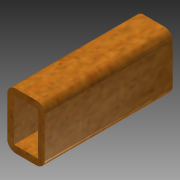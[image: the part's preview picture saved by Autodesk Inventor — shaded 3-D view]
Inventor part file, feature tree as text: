
AUTODESK INVENTOR PART (.ipt)
format: ipt  version: 2015 (Build 190159000, 159)  size: 113,152 bytes
history: native  units: in
note: dims shown in document units (in); Inventor stores cm internally (conversion verified against a paired STEP export)
features: reference x4, sketch x1, plane x1, extrude x1, fillet x1
ambient origin geometry x8: Origin, YZ Plane, XZ Plane, XY Plane, X Axis, Y Axis, Z Axis, Center Point
bodies: Solid1 (feature_tree)
feature tree (8):
  sketch  "Sketch1"  dims[d0=0.1in d1=0.0in d2=0.0in d3=0.125in]
  plane  "Work Plane1"
  extrude  "Extrusion1"  TaperAngle=0.0deg  [1 undecoded]
  fillet  "Fillet1"  Radius=0.125in
  reference  "Reference1"
  reference  "Reference2"
  reference  "Reference3"
  reference  "Reference4"
note: 1 required parameter value undecoded (feature->parameter linkage not recoverable at this tier; creation-order binding heuristic only, values carry confidence <= 0.55)
